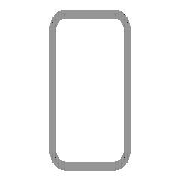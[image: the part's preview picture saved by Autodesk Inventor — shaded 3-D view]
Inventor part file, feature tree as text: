
AUTODESK INVENTOR PART (.ipt)
format: ipt  version: 2025 (Build 290162010, 162A)  size: 151,040 bytes
history: native  units: mm (DEFAULTED — no unit token found)
features: other x4, plane x3, split x2, sketch x1
ambient origin geometry x8: Origin, YZ Plane, XZ Plane, XY Plane, X Axis, Y Axis, Z Axis, Center Point
bodies: Solid1 (feature_tree), Body (feature_tree)
feature tree (10):
  parser-record x1  (decoder bookkeeping rows leaked as tree rows — omitted from the tree; the rows remain in map.json)
  other  "Driven Length"
  other  "Start Plane"
  other  "End Plane"
  plane  "Work Plane4"
  split  "Split1"
  plane  "Work Plane5"
  split  "Split2"
  sketch  "Sketch3"  dims[d3=1700.0mm d4=0.0mm d7=6.0mm d9=40.0mm d11=80.0mm d12=3.0mm d13=-0.0mm d14=1700.0mm d15=20.0mm d16=40.0mm d17=90.0deg d18=1700.0mm]
  plane  "Work Plane3"
